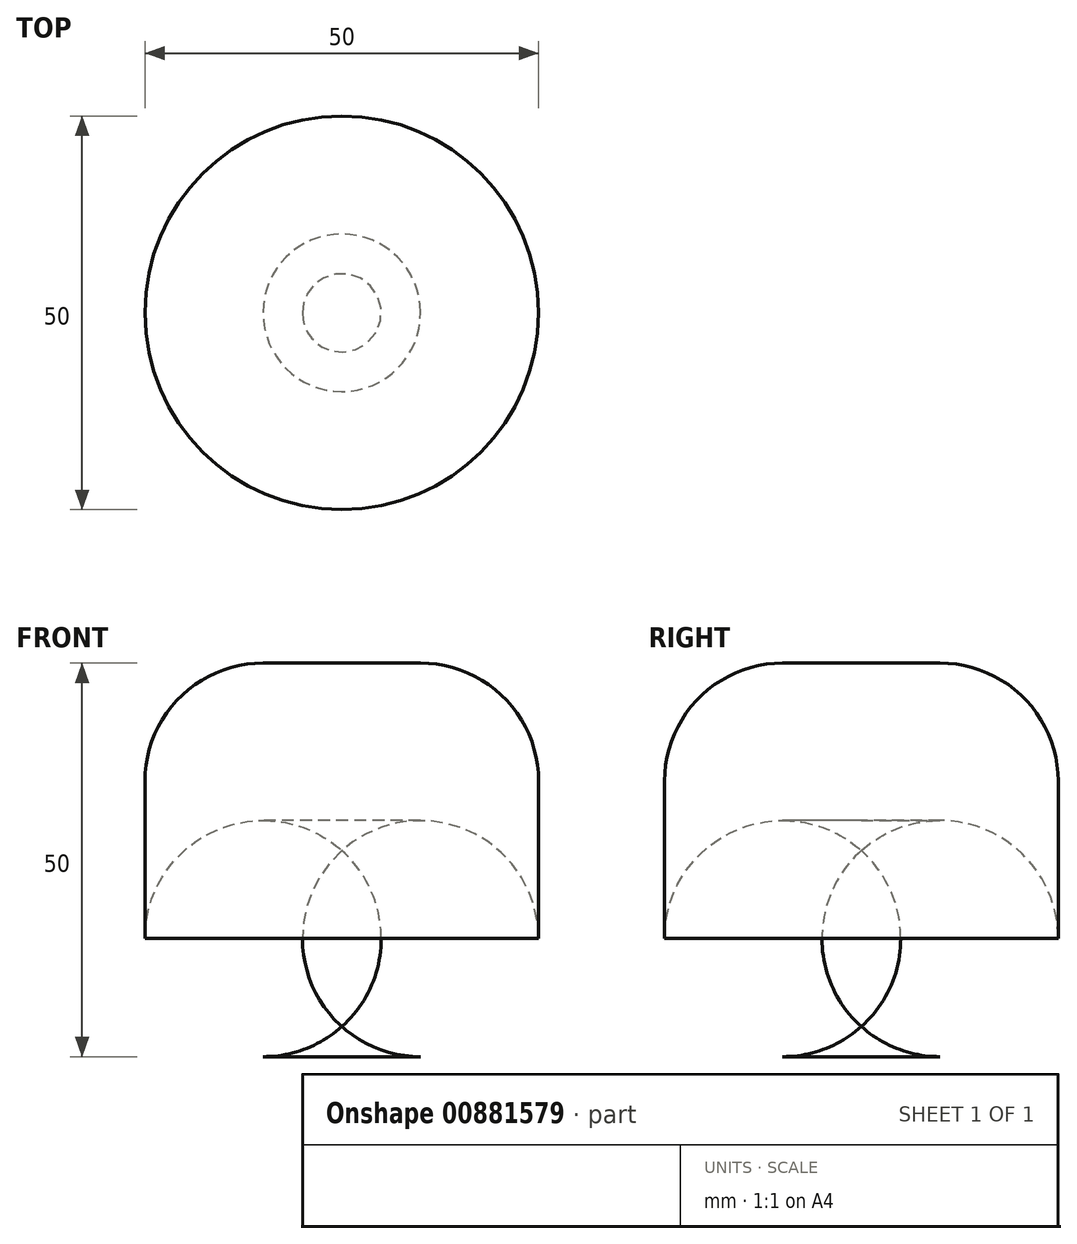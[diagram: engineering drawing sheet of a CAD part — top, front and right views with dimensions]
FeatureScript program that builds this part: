
annotation { "Feature Type Name" : "Feature", "Feature Type Description" : "" }
export const myFeature = defineFeature(function(context is Context, id is Id, definition is map)
    precondition{}
    {
        {
            var Q0;
            Q0=qCreatedBy(makeId("Top.planeOp"),FACE);
            var sketch = newSketch(context, id + "F0", { "sketchPlane" : qUnion([Q0])});
            skCircle(sketch, "E0", {"center": v(0, 0) * mm, "radius": 25 * mm});
            skSolve(sketch);
        }
        {
            var Q0;
            Q0 = qSketchRegion(id + "F0", true);
            extrude(context, id + "F1", {"entities" : qUnion([Q0]), "depth" : 50 * mm, "offsetDistance" : 25 * mm});
        }
        {
            var Q0;
            Q0=makeQuery(id+"F1.opExtrude","CAP_FACE",FACE,{"disambiguationData":[OSD([sQuery(id+"F0.wireOp",EDGE,"E0")])],"isStart":false});
            var Q1;
            Q1=makeQuery(id+"F1.opExtrude","CAP_FACE",FACE,{"disambiguationData":[OSD([sQuery(id+"F0.wireOp",EDGE,"E0")])],"isStart":true});
            fillet(context, id + "F2", {"entities" : qUnion([Q0, Q1]), "radius" : 15 * mm, "tangentPropagation" : true, "allowEdgeOverflow" : false});
        }
    });
